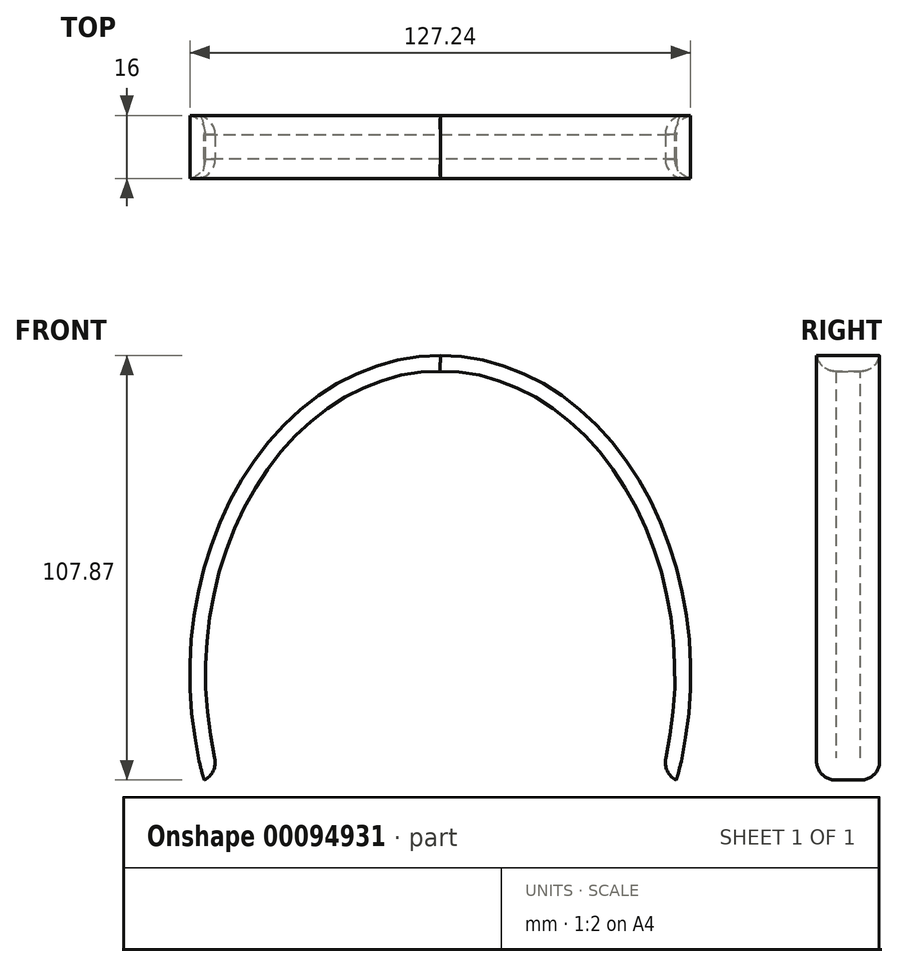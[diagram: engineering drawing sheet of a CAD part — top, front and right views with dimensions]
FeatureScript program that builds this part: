
annotation { "Feature Type Name" : "Feature", "Feature Type Description" : "" }
export const myFeature = defineFeature(function(context is Context, id is Id, definition is map)
    precondition{}
    {
        {
            var Q0;
            Q0=qCreatedBy(makeId("Front.planeOp"),FACE);
            var sketch = newSketch(context, id + "F0", { "sketchPlane" : qUnion([Q0])});
            skFitSpline(sketch, "E0.0", {"points": [v(0, 75.45) * mm, v(-2.48, 75.46) * mm, v(-4.96, 75.28) * mm, v(-7.43, 74.9) * mm, v(-9.9, 74.54) * mm, v(-12.34, 73.99) * mm, v(-14.76, 73.25) * mm, v(-17.19, 72.52) * mm, v(-19.57, 71.6) * mm, v(-21.92, 70.5) * mm, v(-24.27, 69.4) * mm, v(-26.57, 68.12) * mm, v(-28.8, 66.68) * mm, v(-31.04, 65.22) * mm, v(-33.2, 63.6) * mm, v(-35.3, 61.82) * mm, v(-37.4, 60.03) * mm, v(-39.41, 58.1) * mm, v(-41.33, 56) * mm, v(-43.25, 53.9) * mm, v(-45.07, 51.66) * mm, v(-46.79, 49.28) * mm, v(-48.51, 46.9) * mm, v(-50.12, 44.4) * mm, v(-51.6, 41.77) * mm, v(-53.09, 39.14) * mm, v(-54.44, 36.4) * mm, v(-55.68, 33.55) * mm, v(-56.91, 30.7) * mm, v(-58, 27.77) * mm, v(-58.96, 24.77) * mm, v(-59.92, 21.75) * mm, v(-60.73, 18.67) * mm, v(-61.4, 15.53) * mm, v(-62.06, 12.38) * mm, v(-62.58, 9.2) * mm, v(-62.94, 5.98) * mm, v(-63.3, 2.77) * mm, v(-63.51, -0.46) * mm, v(-63.57, -3.73) * mm, v(-63.62, -6.98) * mm, v(-63.52, -10.23) * mm, v(-63.27, -13.47) * mm, v(-63.02, -16.71) * mm, v(-62.62, -19.92) * mm, v(-62.07, -23.1) * mm, v(-61.51, -26.28) * mm, v(-60.81, -29.4) * mm, v(-59.97, -32.46) * mm]});
            skPoint(sketch, "E1.start.orphan", {"position": v(-73.1, 0) * mm});
            skSolve(sketch);
        }
        {
            var Q0;
            Q0=qCreatedBy(makeId("Right.planeOp"),FACE);
            var sketch = newSketch(context, id + "F1", { "sketchPlane" : qUnion([Q0])});
            skLineSegment(sketch, "E2.bottom", {"start": v(8, 71.45) * mm, "end": v(-8, 71.45) * mm});
            skLineSegment(sketch, "E2.left", {"start": v(8, 71.45) * mm, "end": v(8, 75.45) * mm});
            skLineSegment(sketch, "E2.right", {"start": v(-8, 71.45) * mm, "end": v(-8, 75.45) * mm});
            skPoint(sketch, "E2.middle", {"position": v(0, 75.45) * mm});
            skLineSegment(sketch, "E3", {"start": v(-8, 75.45) * mm, "end": v(8, 75.45) * mm});
            skPoint(sketch, "E2.top.end.orphan", {"position": v(-8, 79.45) * mm});
            skPoint(sketch, "E4.orphan", {"position": v(8, 79.45) * mm});
            skSolve(sketch);
        }
        {
            var Q0;
            Q0=makeQuery(id+"F1.imprint","IMPRINT",FACE,{"disambiguationData":[TD([[makeQuery(id+"F1.imprint","IMPRINT",EDGE,{"derivedFrom":sQuery(id+"F1.wireOp",EDGE,"E2.bottom")}),-1.0]])]});
            var Q1;
            Q1=sQuery(id+"F0.wireOp",EDGE,"E0.0");
            sweep(context, id + "F2", {"profiles" : qUnion([Q0]), "path" : qUnion([Q1])});
        }
        {
            var Q0;
            Q0=makeQuery(id+"F2.opSweep","SWEPT_EDGE",EDGE,{"disambiguationData":[OSD([sQuery(id+"F0.wireOp",EDGE,"E0.0"),sQuery(id+"F1.wireOp",EDGE,"E2.bottom"),sQuery(id+"F1.wireOp",EDGE,"E2.right")])]});
            var Q1;
            Q1=makeQuery(id+"F2.opSweep","SWEPT_EDGE",EDGE,{"disambiguationData":[OSD([sQuery(id+"F0.wireOp",EDGE,"E0.0"),sQuery(id+"F1.wireOp",EDGE,"E2.bottom"),sQuery(id+"F1.wireOp",EDGE,"E2.left")])]});
            fillet(context, id + "F3", {"entities" : qUnion([Q0, Q1]), "radius" : 5 * mm, "tangentPropagation" : true, "allowEdgeOverflow" : false});
        }
        {
            var Q0;
            Q0=makeQuery(id+"F2.opSweep","CAP_EDGE",EDGE,{"disambiguationData":[OSD([sQuery(id+"F0.wireOp",VERTEX,"E0.0.end"),sQuery(id+"F1.wireOp",EDGE,"E2.bottom")])],"isStart":false});
            fillet(context, id + "F4", {"entities" : qUnion([Q0]), "radius" : 5 * mm, "tangentPropagation" : true, "allowEdgeOverflow" : false});
        }
        {
            var Q0;
            Q0=makeQuery(id+"F2.opSweep","SWEPT_BODY",BODY,{"disambiguationData":[OSD([sQuery(id+"F0.wireOp",EDGE,"E0.0"),sQuery(id+"F1.wireOp",EDGE,"E2.bottom"),sQuery(id+"F1.wireOp",EDGE,"E2.left"),sQuery(id+"F1.wireOp",EDGE,"E2.right"),sQuery(id+"F1.wireOp",EDGE,"E3")])]});
            var Q1;
            Q1=qCreatedBy(makeId("Right.planeOp"),FACE);
            mirror(context, id + "F5", {"operationType" : NewBodyOperationType.ADD, "entities" : qUnion([Q0]), "mirrorPlane" : qUnion([Q1])});
        }
    });
